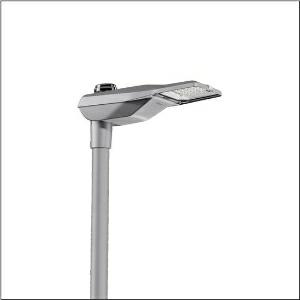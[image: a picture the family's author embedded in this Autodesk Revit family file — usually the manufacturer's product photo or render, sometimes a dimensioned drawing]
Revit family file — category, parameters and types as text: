
# Revit family: streetlight_sl_21_micro___st0_8a_5xe5c47n08cb_5e3b
name_source: partatom
category: Lighting Fixtures
units: mm (PartAtom-declared; Revit-internal decimal feet)

## family parameters
Cut with Voids When Loaded = No
Host = Face
Light Source = No
Part Type = Normal
Room Calculation Point = No
Round Connector Dimension = Use Diameter
Shared = No

## types (1)
- --- (1 x LED, 2380 lm, 15.8 W, 4000K)
    Apparent Load = 16 VA
    CIE Flux Codes = 38 75 97 100 100
    Color Rendering = 70
    Color Temperature = 4000K
    Default Elevation = 1800 mm
    Description = Streetlight SL 21 micro, mast luminaire, primary light control with lens, of PMMA, primary optical cover: cover, of toughened safety glass, transparent, light distribution: ST0.8a, light emission: direct distribution, primary light characteristic: asymmetric, installation type: post-top, LED, 3G 1.5mm², High Power LED, rated luminous flux: 2.380lm, luminous efficacy: 151lm/W, light colour: 740, colour temperature: 4000K, control gear: NEMA (7pin), control: overheat protection, pre-setting: linear dimming characteristic, constant luminous flux control, time-dependent luminous flux control, flexible luminous flux parameterisation, mains connection: 230..240V, AC, 50/60Hz, connection cable pre-assembled, cable length: 6,5m, wiring characteristics: H07RN-F, start of lifetime: 16W, end of service life: 16W, reduction: 8W, luminaire housing, of diecast aluminium (EN AC-44300), powder-coated, Siteco® metallic grey (DB 702S), corrosivity category C5 mid according to DIN EN ISO 12944, multi-level sealing system, sealing non-destructively replaceable, inclination adjustable: 0°, 5°, 10°, 15°, length: 528mm, width: 235mm, height: 110mm, spigot size: 76/60mm (post-top), mounting height: 4..8m, protection rating (complete): IP66, insulation class (complete): insulation class I (protective earthing), certification: CE, ENEC, ENEC+, VDE, impact resistance: IK10, permissible operating ambient temperature for outdoor applications: -40..+50°C, standard-compliant lighting for roads and squares, packaging unit: 1 piece

Light Distribution: ST0.8a
    Height = 110 mm
    Lamp = 1 x LED
    Lamp Light Flux = 2380 lm
    Lamp Power = 15.8 W
    Lamp count = 1
    Length = 528 mm
    Luminous efficacy = 151 lm/W
    Manufacturer = Siteco
    ModVariant = No
    Model = 5XE5C47N08CB
    Number of Poles = 1
    OnlyDefault = Yes
    Power Factor = 1
    Product Name = Streetlight SL 21 micro | ST0.8a
    Product group = mast luminaire | pylon top
    ProductGroupID = 6100
    Protection Class = Protection class I
    Protection Degree = IP 66
    RLX_Detail_Level = 1
    RLX_Emergency_Light_Flux = 0 lm
    RLX_Emergency_Type = 0
    RLX_Emergency_Type_DB = No
    RlxData = <blob elided: 99037 chars, md5=0dc9dd74>
    Socket = socket
    Standby Power = 0 W
    System Light Flux = 2380 lm
    System Power = 16 W
    Type Comments = factory setting: luminous flux: 100 % | dim-lin: 254 | 300 mA
    Type Image = l_1294375.jpg
    URL = http://relux.com
    VarID = @adj_134342
    Voltage = 0 V
    Weight = 0.00 kg
    Width = 235 mm

## geometry (parser evidence)
native form markers: Blend x4, Sweep x9
no freeform markers — native parametric forms only
